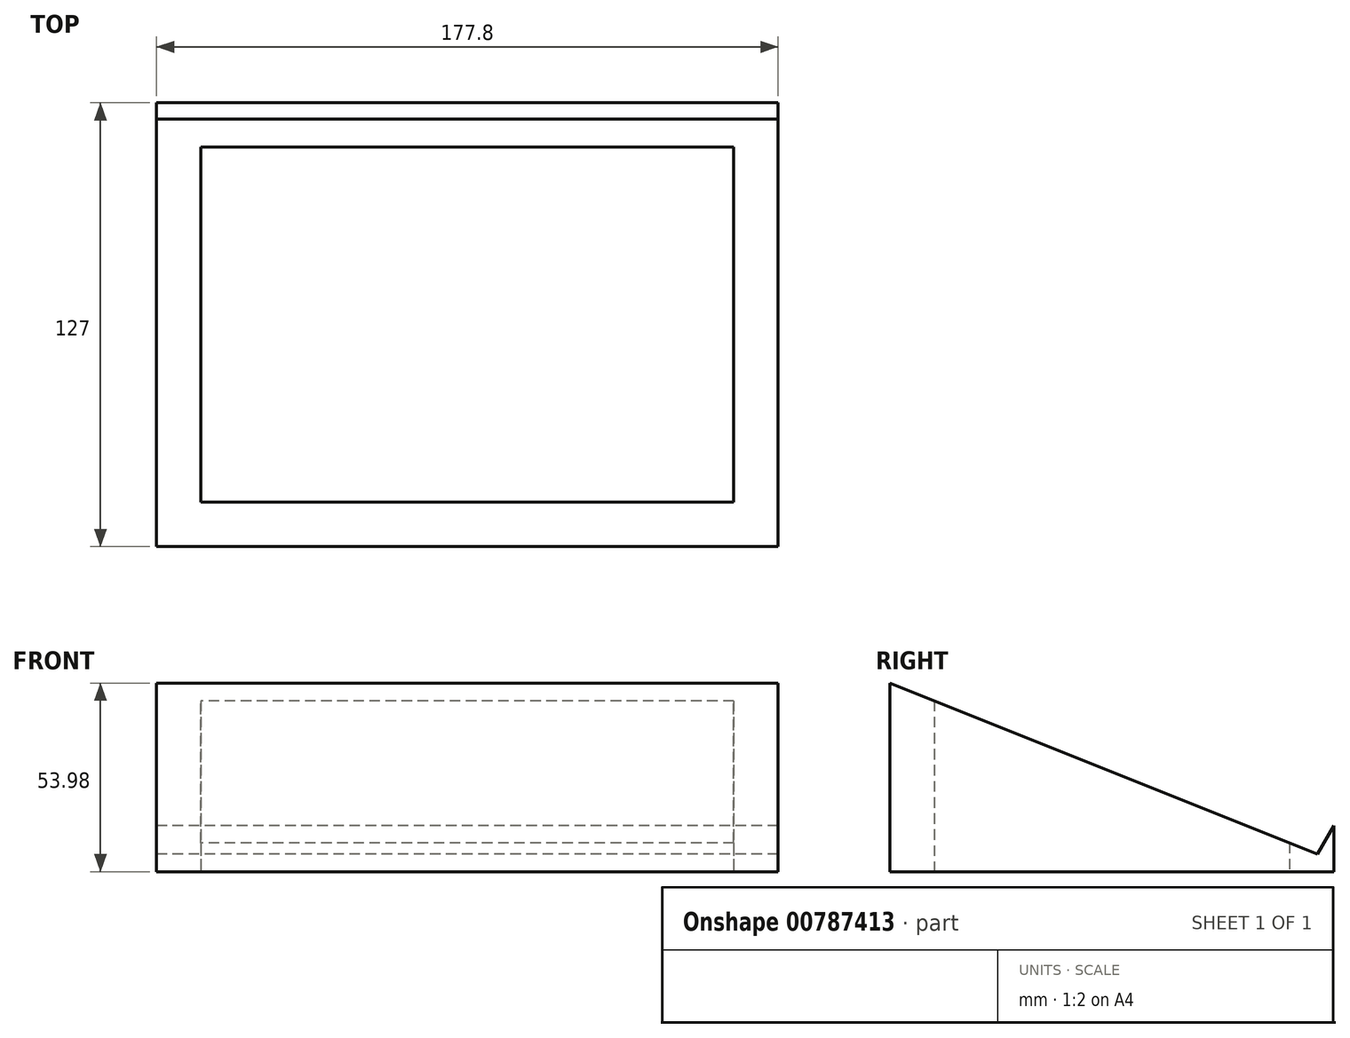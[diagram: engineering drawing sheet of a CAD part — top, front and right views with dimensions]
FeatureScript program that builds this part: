
annotation { "Feature Type Name" : "Feature", "Feature Type Description" : "" }
export const myFeature = defineFeature(function(context is Context, id is Id, definition is map)
    precondition{}
    {
        {
            var Q0;
            Q0=qCreatedBy(makeId("Top.planeOp"),FACE);
            var sketch = newSketch(context, id + "F0", { "sketchPlane" : qUnion([Q0])});
            skLineSegment(sketch, "E0.bottom", {"start": v(88.9, -63.5) * mm, "end": v(-88.9, -63.5) * mm});
            skLineSegment(sketch, "E0.top", {"start": v(88.9, 63.5) * mm, "end": v(-88.9, 63.5) * mm});
            skLineSegment(sketch, "E0.left", {"start": v(88.9, -63.5) * mm, "end": v(88.9, 63.5) * mm});
            skLineSegment(sketch, "E0.right", {"start": v(-88.9, -63.5) * mm, "end": v(-88.9, 63.5) * mm});
            skPoint(sketch, "E0.middle", {"position": v(0, 0) * mm});
            skSolve(sketch);
        }
        {
            var Q0;
            Q0=makeQuery(id+"F0.imprint","IMPRINT",FACE,{"disambiguationData":[TD([[makeQuery(id+"F0.imprint","IMPRINT",EDGE,{"derivedFrom":sQuery(id+"F0.wireOp",EDGE,"E0.bottom")}),-1.0]])]});
            extrude(context, id + "F1", {"entities" : qUnion([Q0]), "depth" : 50.8 * mm, "offsetDistance" : 25.4 * mm});
        }
        {
            var Q0;
            Q0=makeQuery(id+"F1.opExtrude","SWEPT_FACE",FACE,{"disambiguationData":[OSD([sQuery(id+"F0.wireOp",EDGE,"E0.right")])]});
            var sketch = newSketch(context, id + "F2", { "sketchPlane" : qUnion([Q0])});
            skLineSegment(sketch, "E1", {"start": v(-63.5, 0) * mm, "end": v(63.5, 50.8) * mm});
            skLineSegment(sketch, "E2.0.0", {"start": v(-63.5, 0) * mm, "end": v(63.5, 0) * mm});
            skLineSegment(sketch, "E2.0.1", {"start": v(63.5, 0) * mm, "end": v(63.5, 50.8) * mm});
            skPoint(sketch, "E2.0.3.start.orphan", {"position": v(-63.5, 50.8) * mm});
            skLineSegment(sketch, "E3.bottom", {"start": v(-63.5, 0) * mm, "end": v(-57.74, 0) * mm});
            skLineSegment(sketch, "E3.left", {"start": v(-63.5, 0) * mm, "end": v(-63.5, 9.96) * mm});
            skLineSegment(sketch, "E4", {"start": v(-63.5, 9.96) * mm, "end": v(-58.82, 1.87) * mm});
            skSolve(sketch);
        }
        {
            var Q0;
            {var subQ3=sQuery(id+"F2.wireOp",EDGE,"E4");Q0=makeQuery(id+"F2.imprint","IMPRINT",FACE,{"disambiguationData":[TD([[makeQuery(id+"F2.imprint","IMPRINT",EDGE,{"derivedFrom":subQ3}),1.0]])]});}
            extrude(context, id + "F3", {"entities" : qUnion([Q0]), "operationType" : NewBodyOperationType.REMOVE, "oppositeDirection" : true, "depth" : 2514.6 * mm, "offsetDistance" : 25.4 * mm});
        }
        {
            var Q0;
            Q0=makeQuery(id+"F1.opExtrude","CAP_FACE",FACE,{"disambiguationData":[OSD([sQuery(id+"F0.wireOp",EDGE,"E0.bottom"),sQuery(id+"F0.wireOp",EDGE,"E0.top"),sQuery(id+"F0.wireOp",EDGE,"E0.left"),sQuery(id+"F0.wireOp",EDGE,"E0.right")])],"isStart":true});
            extrude(context, id + "F4", {"entities" : qUnion([Q0]), "operationType" : NewBodyOperationType.ADD, "depth" : 3.17 * mm, "offsetDistance" : 25.4 * mm});
        }
        {
            var Q0;
            Q0=makeQuery(id+"F4.opExtrude","CAP_FACE",FACE,{"disambiguationData":[OSD([sQuery(id+"F0.wireOp",EDGE,"E0.bottom"),sQuery(id+"F0.wireOp",EDGE,"E0.top"),sQuery(id+"F0.wireOp",EDGE,"E0.left"),sQuery(id+"F0.wireOp",EDGE,"E0.right")])],"isStart":false});
            var sketch = newSketch(context, id + "F5", { "sketchPlane" : qUnion([Q0])});
            skLineSegment(sketch, "E5.bottom", {"start": v(76.2, -50.8) * mm, "end": v(-76.2, -50.8) * mm});
            skLineSegment(sketch, "E5.top", {"start": v(76.2, 50.8) * mm, "end": v(-76.2, 50.8) * mm});
            skLineSegment(sketch, "E5.left", {"start": v(76.2, -50.8) * mm, "end": v(76.2, 50.8) * mm});
            skLineSegment(sketch, "E5.right", {"start": v(-76.2, -50.8) * mm, "end": v(-76.2, 50.8) * mm});
            skPoint(sketch, "E5.middle", {"position": v(0, 0) * mm});
            skLineSegment(sketch, "E6", {"start": v(0, 50.8) * mm, "end": v(0, 63.5) * mm});
            skLineSegment(sketch, "E7", {"start": v(76.2, 0) * mm, "end": v(88.9, 0) * mm});
            skSolve(sketch);
        }
        {
            var Q0;
            {var subQ1=sQuery(id+"F5.wireOp",EDGE,"E5.bottom");Q0=makeQuery(id+"F5.imprint","IMPRINT",FACE,{"disambiguationData":[TD([[makeQuery(id+"F5.imprint","IMPRINT",EDGE,{"derivedFrom":subQ1}),-1.0]])]});}
            extrude(context, id + "F6", {"entities" : qUnion([Q0]), "operationType" : NewBodyOperationType.REMOVE, "oppositeDirection" : true, "depth" : 2514.6 * mm, "offsetDistance" : 25.4 * mm});
        }
    });
